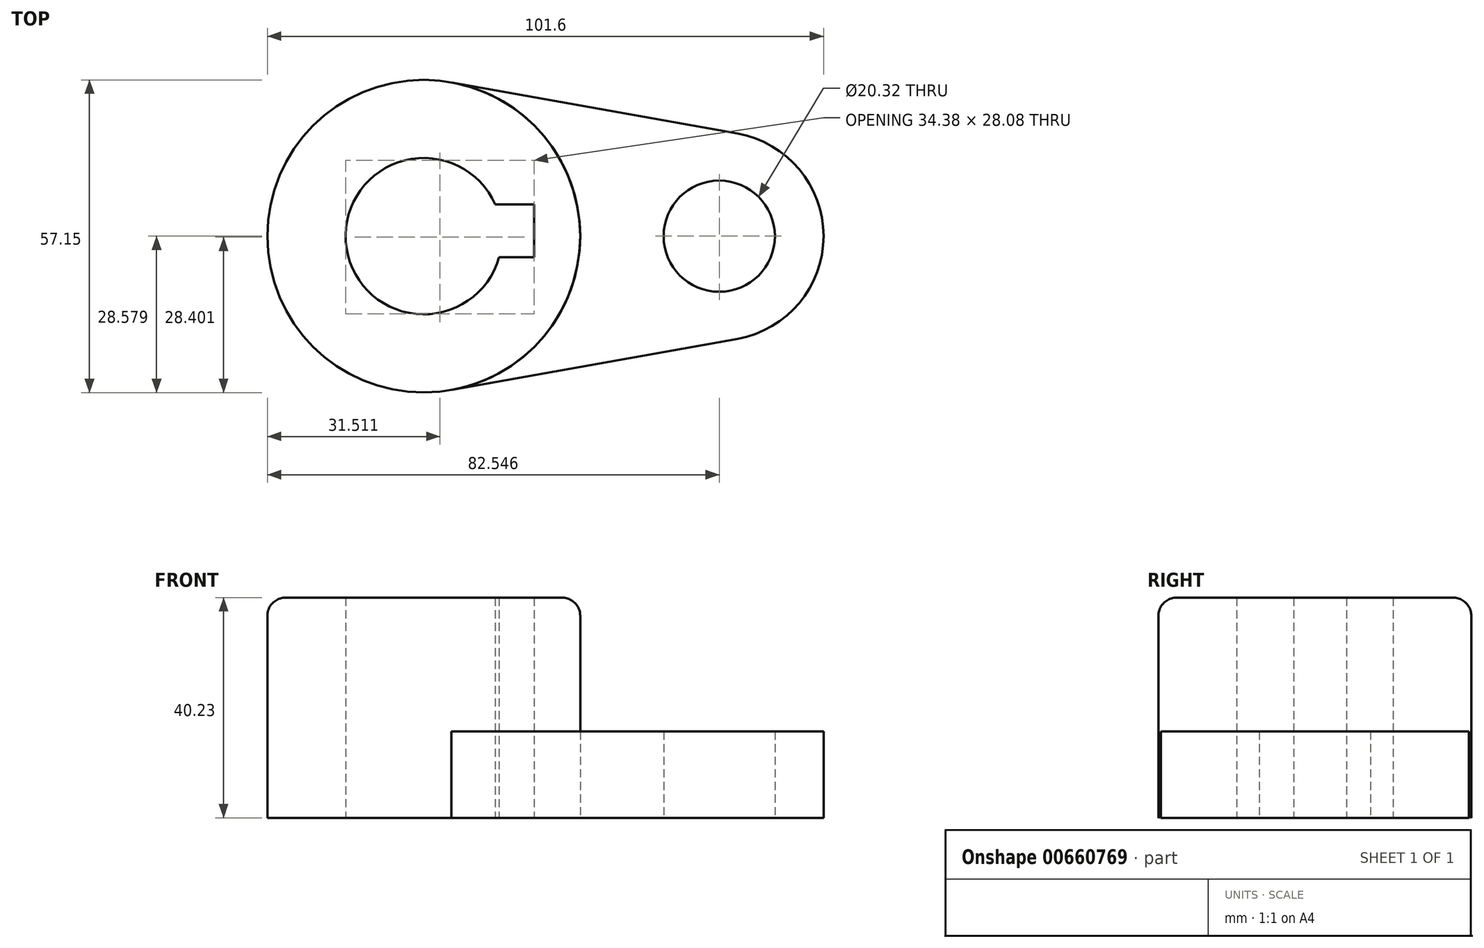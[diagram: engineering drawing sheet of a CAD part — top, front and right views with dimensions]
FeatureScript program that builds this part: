
annotation { "Feature Type Name" : "Feature", "Feature Type Description" : "" }
export const myFeature = defineFeature(function(context is Context, id is Id, definition is map)
    precondition{}
    {
        {
            var Q0;
            Q0=qCreatedBy(makeId("Top.planeOp"),FACE);
            var sketch = newSketch(context, id + "F0", { "sketchPlane" : qUnion([Q0])});
            skCircle(sketch, "E0", {"center": v(-30.88, 6.73) * mm, "radius": 14.29 * mm});
            skCircle(sketch, "E1", {"center": v(23.1, 6.73) * mm, "radius": 10.16 * mm});
            skCircle(sketch, "E2", {"center": v(-30.88, 6.73) * mm, "radius": 28.58 * mm});
            skCircle(sketch, "E3", {"center": v(23.1, 6.73) * mm, "radius": 19.05 * mm});
            skLineSegment(sketch, "E4", {"start": v(-25.84, 34.86) * mm, "end": v(26.46, 25.48) * mm});
            skLineSegment(sketch, "E5", {"start": v(26.46, -12.02) * mm, "end": v(-25.84, -21.4) * mm});
            skLineSegment(sketch, "E6", {"start": v(-10.75, 12.53) * mm, "end": v(-10.75, 2.88) * mm});
            skLineSegment(sketch, "E7", {"start": v(-10.75, 2.88) * mm, "end": v(-17.12, 2.88) * mm});
            skLineSegment(sketch, "E8", {"start": v(-10.75, 12.53) * mm, "end": v(-17.82, 12.53) * mm});
            skSolve(sketch);
        }
        {
            var Q0;
            Q0=makeQuery(id+"F0.imprint","IMPRINT",FACE,{"disambiguationData":[TD([[makeQuery(id+"F0.imprint","IMPRINT",EDGE,{"derivedFrom":sQuery(id+"F0.wireOp",EDGE,"E6")}),1.0]])]});
            extrude(context, id + "F1", {"entities" : qUnion([Q0]), "depth" : 40.23 * mm, "offsetDistance" : 25.4 * mm});
        }
        {
            var Q0;
            {var subQ0=sQuery(id+"F0.wireOp",EDGE,"E4");Q0=makeQuery(id+"F0.imprint","IMPRINT",FACE,{"disambiguationData":[TD([[makeQuery(id+"F0.imprint","IMPRINT",EDGE,{"derivedFrom":subQ0}),-1.0]])]});}
            var Q1;
            Q1=makeQuery(id+"F0.imprint","IMPRINT",FACE,{"disambiguationData":[TD([[makeQuery(id+"F0.imprint","IMPRINT",EDGE,{"derivedFrom":sQuery(id+"F0.wireOp",EDGE,"E1")}),-1.0]])]});
            extrude(context, id + "F2", {"entities" : qUnion([Q0, Q1]), "depth" : 15.77 * mm, "offsetDistance" : 25.4 * mm});
        }
        {
            var Q0;
            Q0=makeQuery(id+"F1.opExtrude","CAP_EDGE",EDGE,{"disambiguationData":[OSD([sQuery(id+"F0.wireOp",EDGE,"E2")])],"isStart":false});
            fillet(context, id + "F3", {"entities" : qUnion([Q0]), "radius" : 3.3 * mm, "tangentPropagation" : true, "allowEdgeOverflow" : false});
        }
    });
